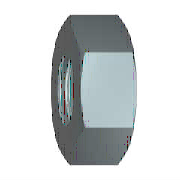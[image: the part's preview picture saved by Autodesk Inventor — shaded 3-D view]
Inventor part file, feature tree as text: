
AUTODESK INVENTOR PART (.ipt)
format: ipt  version: 2013 (Build 170138000, 138)  size: 173,056 bytes
history: native  units: mm (DEFAULTED — no unit token found)
features: sketch x3, chamfer x1, hole x1, other x1, plane x1
ambient origin geometry x7: Origin, YZ Plane, XZ Plane, X Axis, Y Axis, Z Axis, Center Point
bodies: Solid1 (feature_tree), Body (feature_tree)
feature tree (7):
  chamfer  "Chamfer1"  Distance=4.363323mm
  hole  "Thread"  [1 undecoded]
  other  "Work Axis1"
  plane  "Work Plane1"
  sketch  "Sketch1"  dims[d0=12.83161mm]
  sketch  "Sketch2"  dims[d1=5.5626mm]
  sketch  "Sketch3"  dims[d2=0.0mm d3=4.363323mm d4=4.363323mm d5=11.1125mm d6=11.1125mm d7=90.0deg d25=5.3594mm d26=6.0mm d27=4.0mm d28=2.0mm d29=14.3117mm d30=8.0mm d31=20.594885mm d8=0.491005mm d9=30.0deg d10=0.491005mm d11=30.0deg d13=0.0mm d14=0.0mm d39=0.0mm d40=0.491005mm d41=0.491005mm d42=0.0mm]
note: 1 required parameter value undecoded (feature->parameter linkage not recoverable at this tier; creation-order binding heuristic only, values carry confidence <= 0.55)
